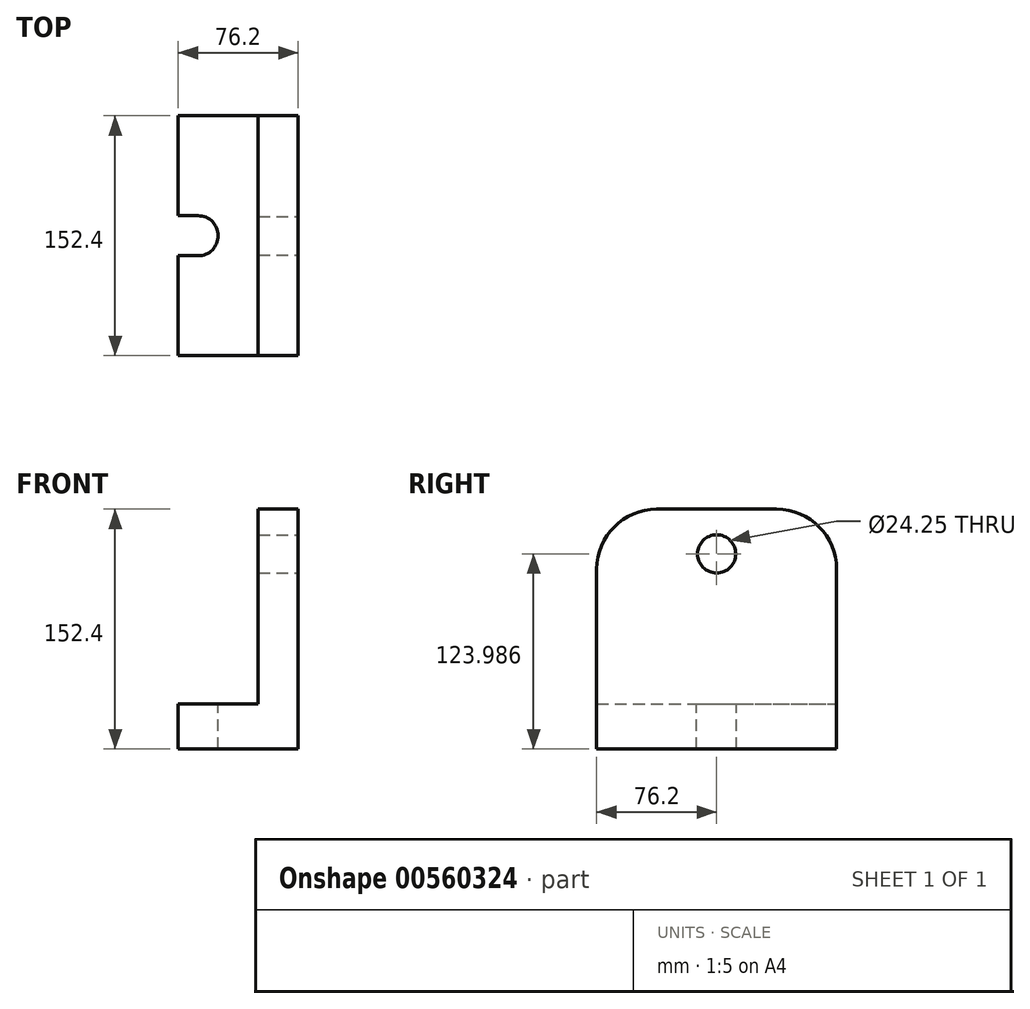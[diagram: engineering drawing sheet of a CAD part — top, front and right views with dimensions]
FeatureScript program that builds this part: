
annotation { "Feature Type Name" : "Feature", "Feature Type Description" : "" }
export const myFeature = defineFeature(function(context is Context, id is Id, definition is map)
    precondition{}
    {
        {
            var Q0;
            Q0=qCreatedBy(makeId("Front.planeOp"),FACE);
            var sketch = newSketch(context, id + "F0", { "sketchPlane" : qUnion([Q0])});
            skLineSegment(sketch, "E0", {"start": v(0, 0) * mm, "end": v(-76.2, 0) * mm});
            skLineSegment(sketch, "E1", {"start": v(0, 0) * mm, "end": v(0, 152.4) * mm});
            skLineSegment(sketch, "E2", {"start": v(0, 152.4) * mm, "end": v(-25.4, 152.4) * mm});
            skLineSegment(sketch, "E3", {"start": v(-25.4, 28.8) * mm, "end": v(-25.4, 152.4) * mm});
            skLineSegment(sketch, "E4", {"start": v(-76.2, 28.8) * mm, "end": v(-25.4, 28.8) * mm});
            skLineSegment(sketch, "E5", {"start": v(-76.2, 28.8) * mm, "end": v(-76.2, 0) * mm});
            skSolve(sketch);
        }
        {
            var Q0;
            Q0=makeQuery(id+"F0.imprint","IMPRINT",FACE,{"disambiguationData":[TD([[makeQuery(id+"F0.imprint","IMPRINT",EDGE,{"derivedFrom":sQuery(id+"F0.wireOp",EDGE,"E0")}),-1.0]])]});
            extrude(context, id + "F1", {"entities" : qUnion([Q0]), "endBound" : BoundingType.SYMMETRIC, "depth" : 152.4 * mm, "offsetDistance" : 25.4 * mm});
        }
        {
            var Q0;
            Q0=makeQuery(id+"F1.opExtrude","SWEPT_FACE",FACE,{"disambiguationData":[OSD([sQuery(id+"F0.wireOp",EDGE,"E1")])]});
            extrude(context, id + "F2", {"entities" : qUnion([Q0]), "operationType" : NewBodyOperationType.REMOVE, "depth" : 25.4 * mm, "offsetDistance" : 25.4 * mm});
        }
        {
            var Q0;
            Q0=makeQuery(id+"F1.opExtrude","SWEPT_FACE",FACE,{"disambiguationData":[OSD([sQuery(id+"F0.wireOp",EDGE,"E1")])]});
            var sketch = newSketch(context, id + "F3", { "sketchPlane" : qUnion([Q0])});
            skCircle(sketch, "E6", {"center": v(0, 123.99) * mm, "radius": 12.12 * mm});
            skSolve(sketch);
        }
        {
            var Q0;
            Q0 = qSketchRegion(id + "F3", true);
            extrude(context, id + "F4", {"entities" : qUnion([Q0]), "operationType" : NewBodyOperationType.REMOVE, "endBound" : BoundingType.THROUGH_ALL, "oppositeDirection" : true, "depth" : 25.4 * mm, "offsetDistance" : 25.4 * mm});
        }
        {
            var Q0;
            Q0=makeQuery(id+"F1.opExtrude","SWEPT_FACE",FACE,{"disambiguationData":[OSD([sQuery(id+"F0.wireOp",EDGE,"E4")])]});
            var sketch = newSketch(context, id + "F5", { "sketchPlane" : qUnion([Q0])});
            skLineSegment(sketch, "E7", {"start": v(-76.2, 12.7) * mm, "end": v(-63.5, 12.7) * mm});
            skArc(sketch, "E8", {"start": v(-63.5, 12.7) * mm, "mid": v(-50.8, 0) * mm, "end": v(-63.5, -12.7) * mm});
            skLineSegment(sketch, "E9", {"start": v(-63.5, -12.7) * mm, "end": v(-76.2, -12.7) * mm});
            skSolve(sketch);
        }
        {
            var Q0;
            Q0 = qSketchRegion(id + "F5", true);
            var Q1;
            {var subQ0=sQuery(id+"F5.wireOp",EDGE,"E7");Q1=makeQuery(id+"F5.imprint","IMPRINT",FACE,{"disambiguationData":[TD([[makeQuery(id+"F5.imprint","IMPRINT",EDGE,{"derivedFrom":subQ0}),-1.0]])]});}
            extrude(context, id + "F6", {"entities" : qUnion([Q0, Q1]), "operationType" : NewBodyOperationType.REMOVE, "endBound" : BoundingType.THROUGH_ALL, "oppositeDirection" : true, "depth" : 25.4 * mm, "offsetDistance" : 25.4 * mm});
        }
        {
            var Q0;
            Q0=makeQuery(id+"F1.opExtrude","SWEPT_FACE",FACE,{"disambiguationData":[OSD([sQuery(id+"F0.wireOp",EDGE,"E3")])]});
            var sketch = newSketch(context, id + "F7", { "sketchPlane" : qUnion([Q0])});
            skArc(sketch, "E10", {"start": v(-38.1, 152.4) * mm, "mid": v(-65.04, 141.24) * mm, "end": v(-76.2, 114.3) * mm});
            skPoint(sketch, "E11", {"position": v(-38.1, 152.4) * mm});
            skPoint(sketch, "E12", {"position": v(-76.2, 114.3) * mm});
            skArc(sketch, "E13", {"start": v(76.2, 114.3) * mm, "mid": v(65.04, 141.24) * mm, "end": v(38.1, 152.4) * mm});
            skLineSegment(sketch, "E14.0", {"start": v(76.2, 152.4) * mm, "end": v(-76.2, 152.4) * mm});
            skLineSegment(sketch, "E15.0", {"start": v(76.2, 28.8) * mm, "end": v(76.2, 152.4) * mm});
            skSolve(sketch);
        }
        {
            var Q0;
            Q0 = qSketchRegion(id + "F7", true);
            var Q1;
            {var subQ0=sQuery(id+"F7.wireOp",EDGE,"E10");Q1=makeQuery(id+"F7.imprint","IMPRINT",FACE,{"disambiguationData":[TD([[makeQuery(id+"F7.imprint","IMPRINT",EDGE,{"derivedFrom":subQ0}),-1.0]])]});}
            extrude(context, id + "F8", {"entities" : qUnion([Q0, Q1]), "operationType" : NewBodyOperationType.REMOVE, "endBound" : BoundingType.THROUGH_ALL, "oppositeDirection" : true, "depth" : 25.4 * mm, "offsetDistance" : 25.4 * mm});
        }
        {
            var Q0;
            Q0=qCreatedBy(makeId("Front.planeOp"),FACE);
            cPlane(context, id + "F9", {"entities" : qUnion([Q0]), "cplaneType" : CPlaneType.OFFSET, "offset" : 44.45 * mm, "width" : 152.4 * mm, "height" : 152.4 * mm});
        }
    });
